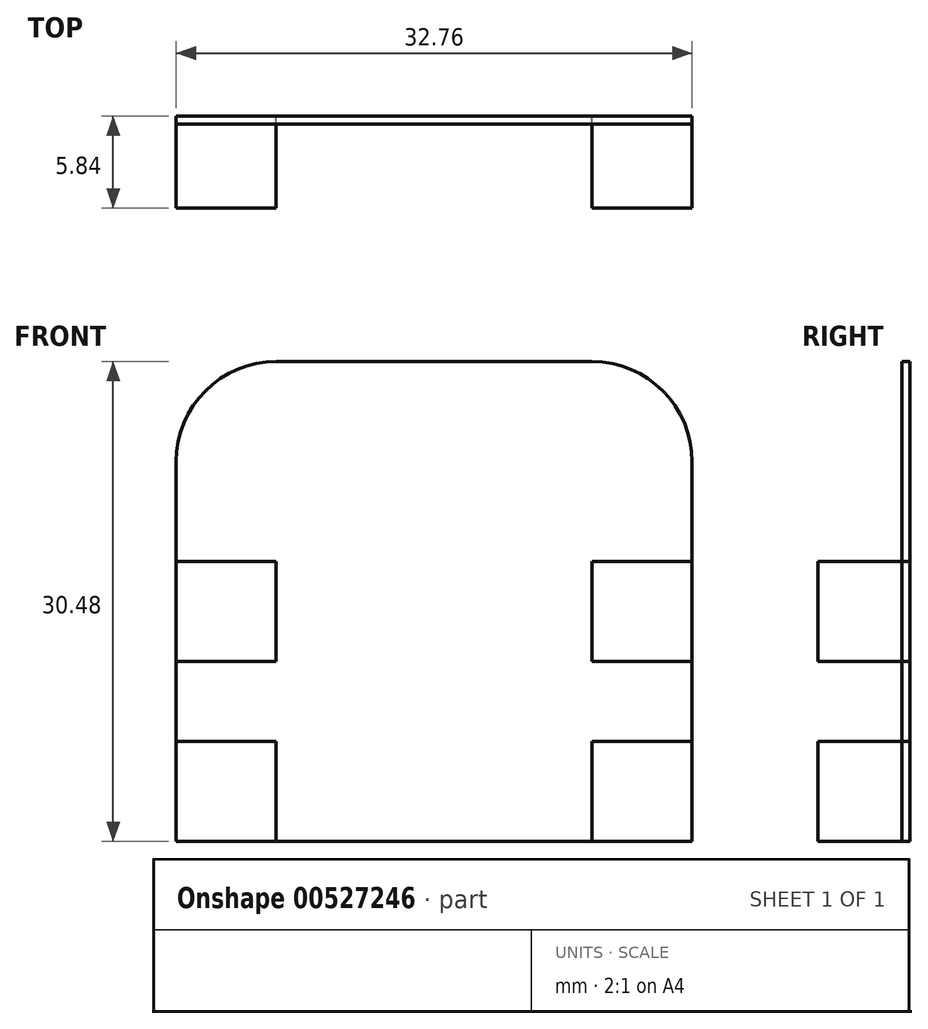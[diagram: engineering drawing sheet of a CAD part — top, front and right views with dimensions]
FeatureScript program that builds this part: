
annotation { "Feature Type Name" : "Feature", "Feature Type Description" : "" }
export const myFeature = defineFeature(function(context is Context, id is Id, definition is map)
    precondition{}
    {
        {
            var Q0;
            Q0=qCreatedBy(makeId("Front.planeOp"),FACE);
            var sketch = newSketch(context, id + "F0", { "sketchPlane" : qUnion([Q0])});
            skLineSegment(sketch, "E0.bottom", {"start": v(16.38, 8.9) * mm, "end": v(-16.38, 8.89) * mm});
            skLineSegment(sketch, "E0.top", {"start": v(16.38, -8.89) * mm, "end": v(-16.38, -8.9) * mm});
            skLineSegment(sketch, "E0.left", {"start": v(16.38, 8.9) * mm, "end": v(16.38, -8.89) * mm});
            skLineSegment(sketch, "E0.right", {"start": v(-16.38, 8.89) * mm, "end": v(-16.38, -8.9) * mm});
            skPoint(sketch, "E0.middle", {"position": v(0, 0) * mm});
            skLineSegment(sketch, "E1.bottom", {"start": v(16.38, 8.9) * mm, "end": v(10.03, 8.9) * mm});
            skLineSegment(sketch, "E1.top", {"start": v(16.38, 2.54) * mm, "end": v(10.03, 2.54) * mm});
            skLineSegment(sketch, "E1.left", {"start": v(16.38, 8.9) * mm, "end": v(16.38, 2.54) * mm});
            skLineSegment(sketch, "E1.right", {"start": v(10.03, 8.9) * mm, "end": v(10.03, 2.54) * mm});
            skLineSegment(sketch, "E2.bottom", {"start": v(-16.38, -8.9) * mm, "end": v(-10.03, -8.9) * mm});
            skLineSegment(sketch, "E2.top", {"start": v(-16.38, -2.54) * mm, "end": v(-10.03, -2.54) * mm});
            skLineSegment(sketch, "E2.left", {"start": v(-16.38, -8.9) * mm, "end": v(-16.38, -2.54) * mm});
            skLineSegment(sketch, "E2.right", {"start": v(-10.03, -8.9) * mm, "end": v(-10.03, -2.54) * mm});
            skLineSegment(sketch, "E3.bottom", {"start": v(-16.38, 8.89) * mm, "end": v(-10.03, 8.89) * mm});
            skLineSegment(sketch, "E3.top", {"start": v(-16.38, 2.54) * mm, "end": v(-10.03, 2.54) * mm});
            skLineSegment(sketch, "E3.left", {"start": v(-16.38, 8.89) * mm, "end": v(-16.38, 2.54) * mm});
            skLineSegment(sketch, "E3.right", {"start": v(-10.03, 8.89) * mm, "end": v(-10.03, 2.54) * mm});
            skLineSegment(sketch, "E4.bottom", {"start": v(16.38, -8.89) * mm, "end": v(10.03, -8.89) * mm});
            skLineSegment(sketch, "E4.top", {"start": v(16.38, -2.54) * mm, "end": v(10.03, -2.54) * mm});
            skLineSegment(sketch, "E4.left", {"start": v(16.38, -8.89) * mm, "end": v(16.38, -2.54) * mm});
            skLineSegment(sketch, "E4.right", {"start": v(10.03, -8.89) * mm, "end": v(10.03, -2.54) * mm});
            skLineSegment(sketch, "E5.bottom", {"start": v(-16.38, 8.89) * mm, "end": v(16.38, 8.89) * mm});
            skLineSegment(sketch, "E5.top", {"start": v(-10.03, 21.59) * mm, "end": v(10.03, 21.59) * mm});
            skLineSegment(sketch, "E5.left", {"start": v(-16.38, 8.89) * mm, "end": v(-16.38, 15.24) * mm});
            skLineSegment(sketch, "E5.right", {"start": v(16.38, 8.89) * mm, "end": v(16.38, 15.24) * mm});
            skPoint(sketch, "E6.visualSharp", {"position": v(-16.38, 21.59) * mm});
            skArc(sketch, "E6.filletArc", {"start": v(-10.03, 21.59) * mm, "mid": v(-14.52, 19.73) * mm, "end": v(-16.38, 15.24) * mm});
            skPoint(sketch, "E7.visualSharp", {"position": v(16.38, 21.59) * mm});
            skArc(sketch, "E7.filletArc", {"start": v(16.38, 15.24) * mm, "mid": v(14.52, 19.73) * mm, "end": v(10.03, 21.59) * mm});
            skSolve(sketch);
        }
        {
            var Q0;
            {var subQ4=sQuery(id+"F0.wireOp",EDGE,"E1.top");Q0=makeQuery(id+"F0.imprint","IMPRINT",FACE,{"disambiguationData":[TD([[makeQuery(id+"F0.imprint","IMPRINT",EDGE,{"derivedFrom":subQ4}),1.0]])]});}
            var Q1;
            Q1=makeQuery(id+"F0.imprint","IMPRINT",FACE,{"disambiguationData":[TD([[makeQuery(id+"F0.imprint","IMPRINT",EDGE,{"derivedFrom":sQuery(id+"F0.wireOp",EDGE,"E5.top")}),-1.0]])]});
            extrude(context, id + "F1", {"entities" : qUnion([Q0, Q1]), "depth" : 0.5 * mm, "offsetDistance" : 25.4 * mm});
        }
        {
            var Q0;
            Q0=makeQuery(id+"F1.opExtrude","CAP_FACE",FACE,{"disambiguationData":[OSD([sQuery(id+"F0.wireOp",EDGE,"E1.top"),sQuery(id+"F0.wireOp",EDGE,"E1.right"),sQuery(id+"F0.wireOp",EDGE,"E2.top"),sQuery(id+"F0.wireOp",EDGE,"E2.right"),sQuery(id+"F0.wireOp",EDGE,"E0.top"),sQuery(id+"F0.wireOp",EDGE,"E0.left"),sQuery(id+"F0.wireOp",EDGE,"E0.right"),sQuery(id+"F0.wireOp",EDGE,"E3.top"),sQuery(id+"F0.wireOp",EDGE,"E3.right"),sQuery(id+"F0.wireOp",EDGE,"E4.top"),sQuery(id+"F0.wireOp",EDGE,"E4.right"),sQuery(id+"F0.wireOp",EDGE,"E5.bottom"),sQuery(id+"F0.wireOp",EDGE,"E5.top"),sQuery(id+"F0.wireOp",EDGE,"E5.left"),sQuery(id+"F0.wireOp",EDGE,"E5.right"),sQuery(id+"F0.wireOp",EDGE,"E6.filletArc"),sQuery(id+"F0.wireOp",EDGE,"E7.filletArc")])],"isStart":false});
            var sketch = newSketch(context, id + "F2", { "sketchPlane" : qUnion([Q0])});
            skLineSegment(sketch, "E8", {"start": v(-16.38, 8.89) * mm, "end": v(-16.38, 2.54) * mm});
            skLineSegment(sketch, "E9", {"start": v(-16.38, -2.54) * mm, "end": v(-16.38, -8.9) * mm});
            skLineSegment(sketch, "E10", {"start": v(-16.38, -8.9) * mm, "end": v(-10.03, -8.9) * mm});
            skLineSegment(sketch, "E11", {"start": v(16.38, 8.89) * mm, "end": v(16.38, 2.54) * mm});
            skLineSegment(sketch, "E12", {"start": v(16.38, -2.54) * mm, "end": v(16.38, -8.89) * mm});
            skLineSegment(sketch, "E13", {"start": v(16.38, -8.89) * mm, "end": v(10.03, -8.89) * mm});
            skSolve(sketch);
        }
        {
            var Q0;
            Q0=makeQuery(id+"F2.imprint","IMPRINT",FACE,{"disambiguationData":[TD([[makeQuery(id+"F2.imprint","IMPRINT",EDGE,{"derivedFrom":sQuery(id+"F2.wireOp",EDGE,"E8")}),1.0]])]});
            var Q1;
            Q1=makeQuery(id+"F2.imprint","IMPRINT",FACE,{"disambiguationData":[TD([[makeQuery(id+"F2.imprint","IMPRINT",EDGE,{"derivedFrom":sQuery(id+"F2.wireOp",EDGE,"E9")}),1.0]])]});
            var Q2;
            Q2=makeQuery(id+"F2.imprint","IMPRINT",FACE,{"disambiguationData":[TD([[makeQuery(id+"F2.imprint","IMPRINT",EDGE,{"derivedFrom":sQuery(id+"F2.wireOp",EDGE,"E12")}),-1.0]])]});
            var Q3;
            Q3=makeQuery(id+"F2.imprint","IMPRINT",FACE,{"disambiguationData":[TD([[makeQuery(id+"F2.imprint","IMPRINT",EDGE,{"derivedFrom":sQuery(id+"F2.wireOp",EDGE,"E11")}),-1.0]])]});
            extrude(context, id + "F3", {"entities" : qUnion([Q0, Q1, Q2, Q3]), "depth" : 5.33 * mm, "offsetDistance" : 25.4 * mm});
        }
    });
